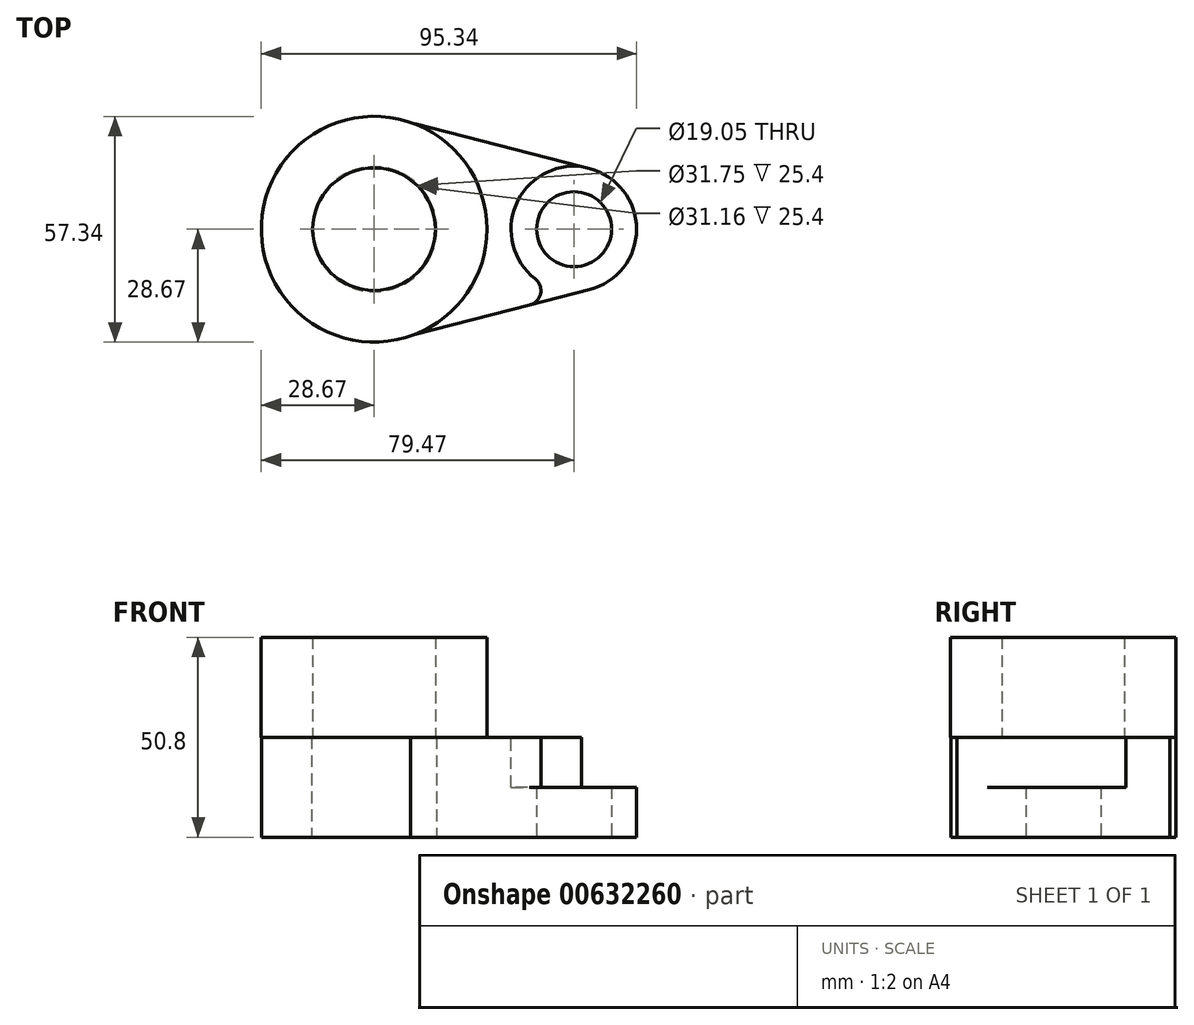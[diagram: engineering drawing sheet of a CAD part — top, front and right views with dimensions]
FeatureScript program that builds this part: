
annotation { "Feature Type Name" : "Feature", "Feature Type Description" : "" }
export const myFeature = defineFeature(function(context is Context, id is Id, definition is map)
    precondition{}
    {
        {
            var Q0;
            Q0=qCreatedBy(makeId("Top.planeOp"),FACE);
            var sketch = newSketch(context, id + "F0", { "sketchPlane" : qUnion([Q0])});
            skCircle(sketch, "E0", {"center": v(0, 0) * mm, "radius": 15.88 * mm});
            skCircle(sketch, "E1", {"center": v(0, 0) * mm, "radius": 28.58 * mm});
            skCircle(sketch, "E2", {"center": v(50.8, 0) * mm, "radius": 9.53 * mm});
            skCircle(sketch, "E3", {"center": v(50.8, 0) * mm, "radius": 15.88 * mm});
            skLineSegment(sketch, "E4", {"start": v(4.9, 28.15) * mm, "end": v(54.74, 15.38) * mm});
            skLineSegment(sketch, "E5", {"start": v(4.9, -28.15) * mm, "end": v(54.74, -15.38) * mm});
            skLineSegment(sketch, "E6.trimOffspring", {"start": v(28.58, 0) * mm, "end": v(34.93, 0) * mm});
            skSolve(sketch);
        }
        {
            var Q0;
            Q0 = qSketchRegion(id + "F0", true);
            extrude(context, id + "F1", {"entities" : qUnion([Q0]), "depth" : 25.4 * mm, "offsetDistance" : 25.4 * mm});
        }
        {
            var Q0;
            Q0=makeQuery(id+"F1.opExtrude","CAP_FACE",FACE,{"disambiguationData":[OSD([sQuery(id+"F0.wireOp",EDGE,"E0"),sQuery(id+"F0.wireOp",EDGE,"E1"),sQuery(id+"F0.wireOp",EDGE,"E2"),sQuery(id+"F0.wireOp",EDGE,"E3"),sQuery(id+"F0.wireOp",EDGE,"E5"),sQuery(id+"F0.wireOp",EDGE,"E4")])],"isStart":false});
            var sketch = newSketch(context, id + "F2", { "sketchPlane" : qUnion([Q0])});
            skCircle(sketch, "E7", {"center": v(0, 0) * mm, "radius": 28.67 * mm});
            skCircle(sketch, "E8", {"center": v(0, 0) * mm, "radius": 15.58 * mm});
            skSolve(sketch);
        }
        {
            var Q0;
            Q0 = qSketchRegion(id + "F2", true);
            extrude(context, id + "F3", {"entities" : qUnion([Q0]), "operationType" : NewBodyOperationType.ADD, "depth" : 25.4 * mm, "offsetDistance" : 25.4 * mm});
        }
        {
            var Q0;
            Q0=makeQuery(id+"F1.opExtrude","CAP_FACE",FACE,{"disambiguationData":[OSD([sQuery(id+"F0.wireOp",EDGE,"E0"),sQuery(id+"F0.wireOp",EDGE,"E1"),sQuery(id+"F0.wireOp",EDGE,"E2"),sQuery(id+"F0.wireOp",EDGE,"E3"),sQuery(id+"F0.wireOp",EDGE,"E5"),sQuery(id+"F0.wireOp",EDGE,"E4")])],"isStart":false});
            var sketch = newSketch(context, id + "F4", { "sketchPlane" : qUnion([Q0])});
            skCircle(sketch, "E9", {"center": v(50.8, 0) * mm, "radius": 9.45 * mm});
            skCircle(sketch, "E10", {"center": v(50.8, 0) * mm, "radius": 16.01 * mm});
            skSolve(sketch);
        }
        {
            var Q0;
            Q0 = qSketchRegion(id + "F4", true);
            extrude(context, id + "F5", {"entities" : qUnion([Q0]), "operationType" : NewBodyOperationType.REMOVE, "oppositeDirection" : true, "depth" : 12.7 * mm, "offsetDistance" : 25.4 * mm});
        }
        {
            var Q0;
            Q0=makeQuery(id+"F5.boolean.opBoolean","INTERSECT",EDGE,{"derivedFrom":[makeQuery(id+"F1.opExtrude","SWEPT_FACE",FACE,{"disambiguationData":[OSD([sQuery(id+"F0.wireOp",EDGE,"E5")])]}),makeQuery(id+"F5.opExtrude","SWEPT_FACE",FACE,{"disambiguationData":[OSD([sQuery(id+"F4.wireOp",EDGE,"E10")])]})]});
            var Q1;
            Q1=makeQuery(id+"F5.boolean.opBoolean","INTERSECT",EDGE,{"derivedFrom":[makeQuery(id+"F1.opExtrude","SWEPT_FACE",FACE,{"disambiguationData":[OSD([sQuery(id+"F0.wireOp",EDGE,"E4")])]}),makeQuery(id+"F5.opExtrude","SWEPT_FACE",FACE,{"disambiguationData":[OSD([sQuery(id+"F4.wireOp",EDGE,"E10")])]})]});
            fillet(context, id + "F6", {"entities" : qUnion([Q0, Q1]), "radius" : 3.8 * mm, "tangentPropagation" : true, "allowEdgeOverflow" : false});
        }
    });
